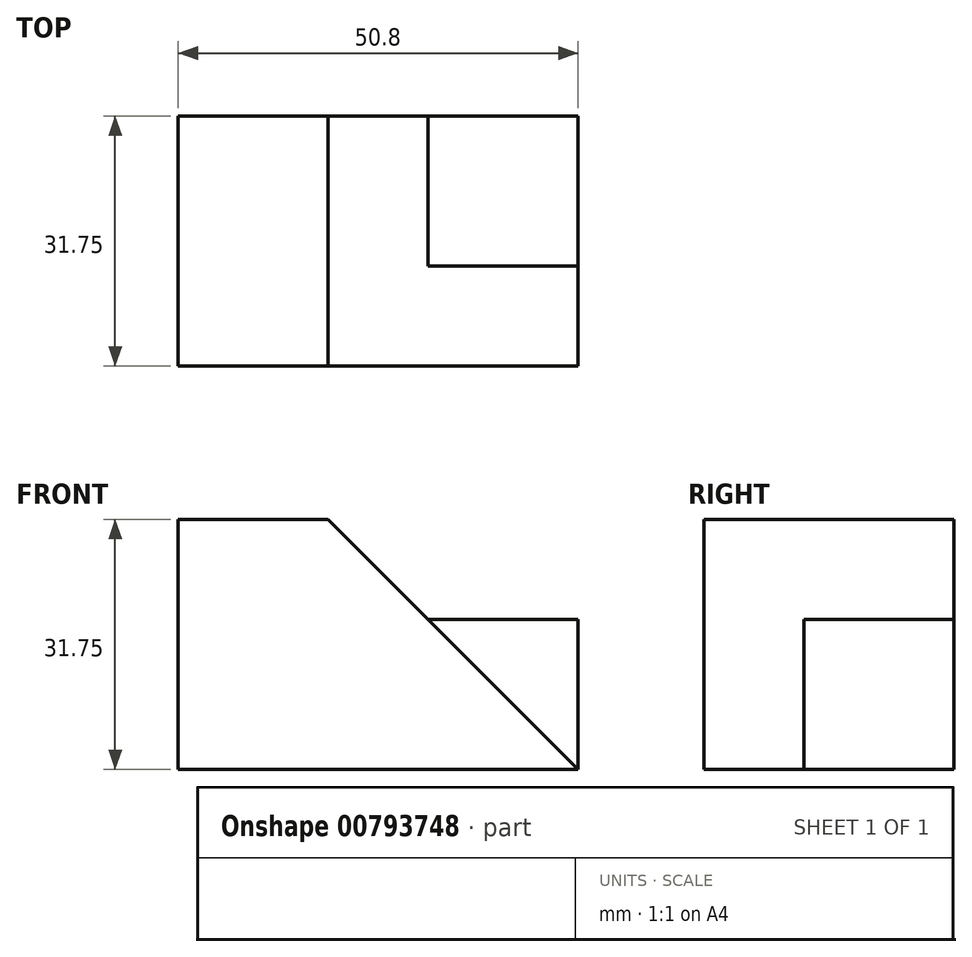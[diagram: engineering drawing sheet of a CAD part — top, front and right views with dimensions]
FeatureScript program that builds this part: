
annotation { "Feature Type Name" : "Feature", "Feature Type Description" : "" }
export const myFeature = defineFeature(function(context is Context, id is Id, definition is map)
    precondition{}
    {
        {
            var Q0;
            Q0=qCreatedBy(makeId("Front.planeOp"),FACE);
            var sketch = newSketch(context, id + "F0", { "sketchPlane" : qUnion([Q0])});
            skLineSegment(sketch, "E0", {"start": v(0, 0) * mm, "end": v(0, 31.75) * mm});
            skLineSegment(sketch, "E1", {"start": v(0, 31.75) * mm, "end": v(19.05, 31.75) * mm});
            skLineSegment(sketch, "E2", {"start": v(0, 0) * mm, "end": v(50.8, 0) * mm});
            skLineSegment(sketch, "E3", {"start": v(19.05, 31.75) * mm, "end": v(50.8, 0) * mm});
            skLineSegment(sketch, "E4", {"start": v(50.8, 0) * mm, "end": v(50.8, 19.05) * mm});
            skLineSegment(sketch, "E5", {"start": v(50.8, 19.05) * mm, "end": v(31.75, 19.05) * mm});
            skSolve(sketch);
        }
        {
            var Q0;
            Q0=makeQuery(id+"F0.imprint","IMPRINT",FACE,{"disambiguationData":[TD([[makeQuery(id+"F0.imprint","IMPRINT",EDGE,{"derivedFrom":sQuery(id+"F0.wireOp",EDGE,"E0")}),-1.0]])]});
            var Q1;
            {var subQ0=sQuery(id+"F0.wireOp",EDGE,"E4");Q1=makeQuery(id+"F0.imprint","IMPRINT",FACE,{"disambiguationData":[TD([[makeQuery(id+"F0.imprint","IMPRINT",EDGE,{"derivedFrom":subQ0}),1.0]])]});}
            extrude(context, id + "F1", {"entities" : qUnion([Q0, Q1]), "depth" : 31.75 * mm, "offsetDistance" : 25.4 * mm});
        }
        {
            var Q0;
            Q0=makeQuery(id+"F1.opExtrude","CAP_FACE",FACE,{"disambiguationData":[OSD([sQuery(id+"F0.wireOp",EDGE,"E0"),sQuery(id+"F0.wireOp",EDGE,"E1"),sQuery(id+"F0.wireOp",EDGE,"E2"),sQuery(id+"F0.wireOp",EDGE,"E3"),sQuery(id+"F0.wireOp",EDGE,"E4"),sQuery(id+"F0.wireOp",EDGE,"E5")])],"isStart":false});
            var sketch = newSketch(context, id + "F2", { "sketchPlane" : qUnion([Q0])});
            skLineSegment(sketch, "E6", {"start": v(31.75, 19.05) * mm, "end": v(50.8, 0) * mm});
            skSolve(sketch);
        }
        {
            var Q0;
            Q0=makeQuery(id+"F2.imprint","IMPRINT",FACE,{"disambiguationData":[TD([[makeQuery(id+"F2.imprint","IMPRINT",EDGE,{"derivedFrom":sQuery(id+"F2.wireOp",EDGE,"E6")}),1.0]])]});
            extrude(context, id + "F3", {"entities" : qUnion([Q0]), "operationType" : NewBodyOperationType.REMOVE, "oppositeDirection" : true, "depth" : 12.7 * mm, "offsetDistance" : 25.4 * mm});
        }
    });
